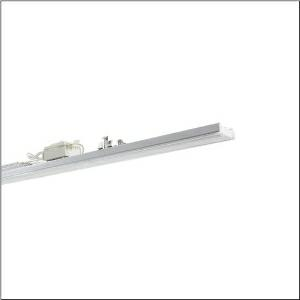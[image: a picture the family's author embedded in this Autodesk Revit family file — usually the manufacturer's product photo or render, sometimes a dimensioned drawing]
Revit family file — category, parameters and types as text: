
# Revit family: licross_21_recessed_mo_52tl12cn49xg
name_source: partatom
category: Lighting Fixtures
units: mm (PartAtom-declared; Revit-internal decimal feet)

## family parameters
Cut with Voids When Loaded = No
Host = Face
Light Source = No
Part Type = Normal
Room Calculation Point = No
Round Connector Dimension = Use Diameter
Shared = No

## types (1)
- --- (1 x LED, 9260 lm, 49.9 W, 4000K)
    Apparent Load = 50 VA
    CIE Flux Codes = 72 92 99 100 100
    Color Rendering = 80
    Color Temperature = 4000K
    Default Elevation = 1800 mm
    Description = Licross 21 Recessed MO, luminaire insert, of sheet steel, galvanised, coil coated, white, length: 1.500mm, width: 66mm, height: 67mm, LED rated luminous flux: 9.260lm, light colour: 840, SDCM (Standard Deviation of Colour Matching)MacAdam ≤ 3 SDCM (initial), control gear: ON/OFF Multilumen, CLOi, with plug, 3-pole, with phase selection, mains connection: 220..240V, AC, 50/60Hz, start of lifetime: 50W, end of service life: 61W, internal wiring halogen-free, primary optical cover: cover, of PMMA, light emission: direct distribution, primary light characteristic: symmetric, protection rating (complete): IP40, insulation class (complete): insulation class I (protective earthing), certification: CE, ENEC, VDE, UKCA, protection symbol: D if used in an environment without relevant dust loads with corresponding accessories, impact resistance: IK06, permissible ambient temperature for indoor applications: -35..+40°C, corresponds to IFS (International Featured Standards) requirements for safety and quality in the food industry, reducing of maximum allowable ambient temperature of 5°C with ceiling mounting, LABS conformity tested according to VDMA 24364:2018-05, The light source and the operating device comply with the requirements of the Ecodesign Regulation (EU) 2019/2020 and are replaceable in accordance with this regulation, packaging unit: 1 piece
    Height = 58 mm
    Lamp = 1 x LED
    Lamp Light Flux = 9260 lm
    Lamp Power = 49.9 W
    Lamp count = 1
    Length = 1500 mm
    Luminous efficacy = 186 lm/W
    Manufacturer = Siteco
    ModVariant = No
    Model = 52TL12CN49XG
    Mounting Place = Ceiling
    Mounting Type = Pendant
    Number of Poles = 1
    OnlyDefault = Yes
    Power Factor = 1
    Product Name = Licross 21 Recessed MO
    Product group = luminaire insert | ceiling pendant
    ProductGroupID = 901
    Protection Class = Protection class I
    Protection Degree = IP 40
    RLX_Detail_Level = 1
    RLX_Emergency_Light_Flux = 0 lm
    RLX_Emergency_Type = 0
    RLX_Emergency_Type_DB = No
    RlxData = <blob elided: 22625 chars, md5=4b497d08>
    Socket = socket
    Standby Power = 0 W
    System Light Flux = 9260 lm
    System Power = 50 W
    Type Comments = factory setting: luminous flux: 100 % | (A | C | E) | 116 mA
    Type Image = l_1296930.jpg
    URL = http://relux.com
    VarID = @adj_110557
    Voltage = 0 V
    Weight = 0.00 kg
    Width = 66 mm

## geometry (parser evidence)
native form markers: Blend x4, Sweep x11
no freeform markers — native parametric forms only
